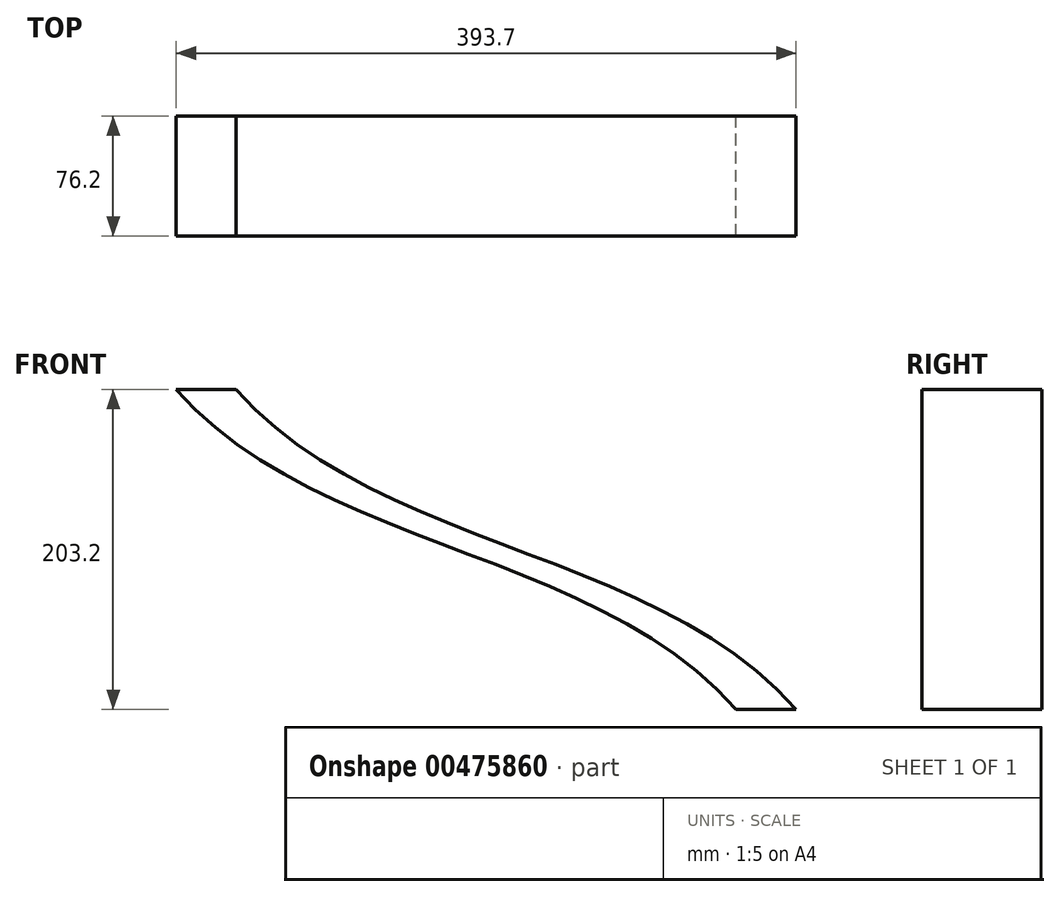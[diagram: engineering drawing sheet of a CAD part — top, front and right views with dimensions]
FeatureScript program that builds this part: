
annotation { "Feature Type Name" : "Feature", "Feature Type Description" : "" }
export const myFeature = defineFeature(function(context is Context, id is Id, definition is map)
    precondition{}
    {
        {
            var Q0;
            Q0=qCreatedBy(makeId("Front.planeOp"),FACE);
            var sketch = newSketch(context, id + "F0", { "sketchPlane" : qUnion([Q0])});
            skLineSegment(sketch, "E0", {"start": v(87.97, -54.47) * mm, "end": v(126.07, -54.47) * mm});
            skFitSpline(sketch, "E1", {"points": [v(-229.53, 148.73) * mm, v(126.07, -54.47) * mm], "startDerivative": vector(266.7, -304.8) * mm, "endDerivative": vector(266.7, -304.8) * mm});
            skPoint(sketch, "E2.endSnap0", {"position": v(-51.73, -54.47) * mm});
            skLineSegment(sketch, "E3", {"start": v(37.17, 47.13) * mm, "end": v(37.17, -54.47) * mm});
            skFitSpline(sketch, "E4", {"points": [v(-229.53, 148.73) * mm, v(126.07, -54.47) * mm], "startDerivative": vector(533.4, -152.4) * mm, "endDerivative": vector(266.7, -304.8) * mm});
            skSolve(sketch);
        }
        {
            var Q0;
            Q0=qCreatedBy(makeId("Top.planeOp"),FACE);
            var sketch = newSketch(context, id + "F1", { "sketchPlane" : qUnion([Q0])});
            skLineSegment(sketch, "E5.bottom", {"start": v(77.35, -38.1) * mm, "end": v(39.25, -38.1) * mm});
            skLineSegment(sketch, "E5.top", {"start": v(77.35, 38.1) * mm, "end": v(39.25, 38.1) * mm});
            skLineSegment(sketch, "E5.left", {"start": v(77.35, -38.1) * mm, "end": v(77.35, 38.1) * mm});
            skLineSegment(sketch, "E5.right", {"start": v(39.25, -38.1) * mm, "end": v(39.25, 38.1) * mm});
            skPoint(sketch, "E5.middle", {"position": v(58.3, 0) * mm});
            skSolve(sketch);
        }
        {
            var Q0;
            Q0=makeQuery(id+"F1.imprint","IMPRINT",FACE,{"disambiguationData":[TD([[makeQuery(id+"F1.imprint","IMPRINT",EDGE,{"derivedFrom":sQuery(id+"F1.wireOp",EDGE,"E5.bottom")}),-1.0]])]});
            extrude(context, id + "F2", {"entities" : qUnion([Q0]), "depth" : 203.2 * mm});
        }
        {
            var Q0;
            Q0=makeQuery(id+"F2.opExtrude","CAP_FACE",FACE,{"disambiguationData":[OSD([sQuery(id+"F1.wireOp",EDGE,"E5.bottom"),sQuery(id+"F1.wireOp",EDGE,"E5.top"),sQuery(id+"F1.wireOp",EDGE,"E5.left"),sQuery(id+"F1.wireOp",EDGE,"E5.right")])],"isStart":false});
            var Q1;
            Q1=sQuery(id+"F0.wireOp",EDGE,"E1");
            sweep(context, id + "F3", {"profiles" : qUnion([Q0]), "path" : qUnion([Q1]), "keepProfileOrientation" : true});
        }
        {
            var Q0;
            Q0=makeQuery(id+"F2.opExtrude","SWEPT_BODY",BODY,{"disambiguationData":[OSD([sQuery(id+"F1.wireOp",EDGE,"E5.bottom"),sQuery(id+"F1.wireOp",EDGE,"E5.top"),sQuery(id+"F1.wireOp",EDGE,"E5.left"),sQuery(id+"F1.wireOp",EDGE,"E5.right")])]});
            deleteBodies(context, id + "F4", {"entities" : qUnion([Q0])});
        }
    });
